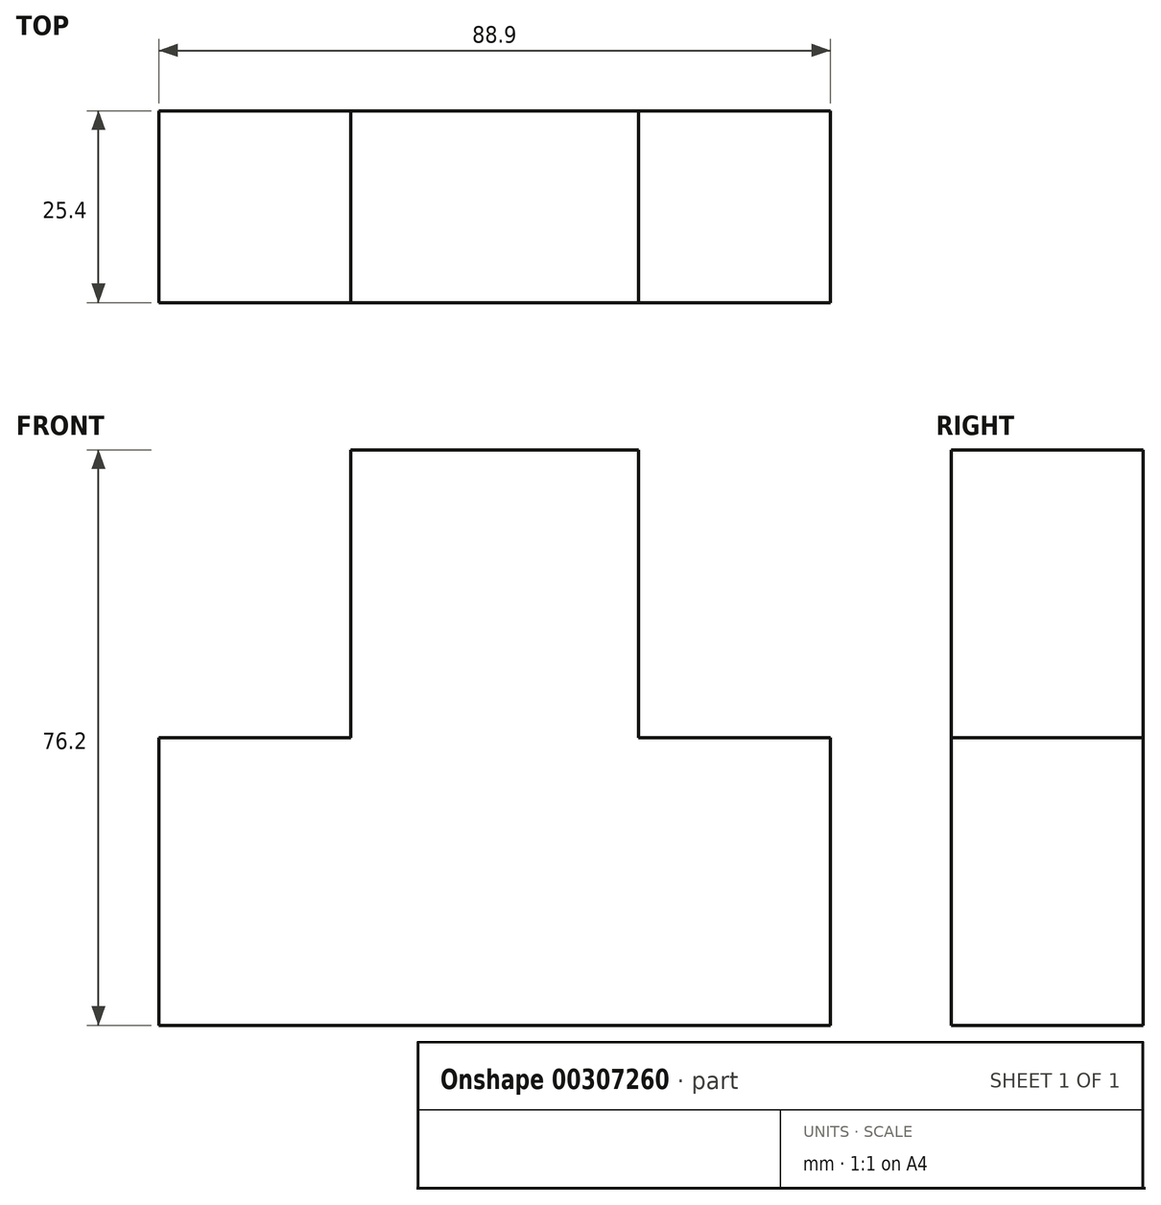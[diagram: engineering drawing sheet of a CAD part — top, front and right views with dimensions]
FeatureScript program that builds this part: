
annotation { "Feature Type Name" : "Feature", "Feature Type Description" : "" }
export const myFeature = defineFeature(function(context is Context, id is Id, definition is map)
    precondition{}
    {
        {
            var Q0;
            Q0=qCreatedBy(makeId("Front.planeOp"),FACE);
            var sketch = newSketch(context, id + "F0", { "sketchPlane" : qUnion([Q0])});
            skLineSegment(sketch, "E0", {"start": v(-46.34, -62.08) * mm, "end": v(42.56, -62.08) * mm});
            skLineSegment(sketch, "E1", {"start": v(42.56, -62.08) * mm, "end": v(42.56, -23.98) * mm});
            skLineSegment(sketch, "E2", {"start": v(42.56, -23.98) * mm, "end": v(17.16, -23.98) * mm});
            skLineSegment(sketch, "E3", {"start": v(17.16, -23.98) * mm, "end": v(17.16, 14.12) * mm});
            skLineSegment(sketch, "E4", {"start": v(17.16, 14.12) * mm, "end": v(-20.94, 14.12) * mm});
            skLineSegment(sketch, "E5", {"start": v(-20.94, 14.12) * mm, "end": v(-20.94, -23.98) * mm});
            skLineSegment(sketch, "E6", {"start": v(-20.94, -23.98) * mm, "end": v(-46.34, -23.98) * mm});
            skLineSegment(sketch, "E7", {"start": v(-46.34, -62.08) * mm, "end": v(-46.34, -23.98) * mm});
            skSolve(sketch);
        }
        {
            var Q0;
            Q0=makeQuery(id+"F0.imprint","IMPRINT",FACE,{"disambiguationData":[TD([[makeQuery(id+"F0.imprint","IMPRINT",EDGE,{"derivedFrom":sQuery(id+"F0.wireOp",EDGE,"E0")}),1.0]])]});
            extrude(context, id + "F1", {"entities" : qUnion([Q0]), "depth" : 25.4 * mm});
        }
    });
